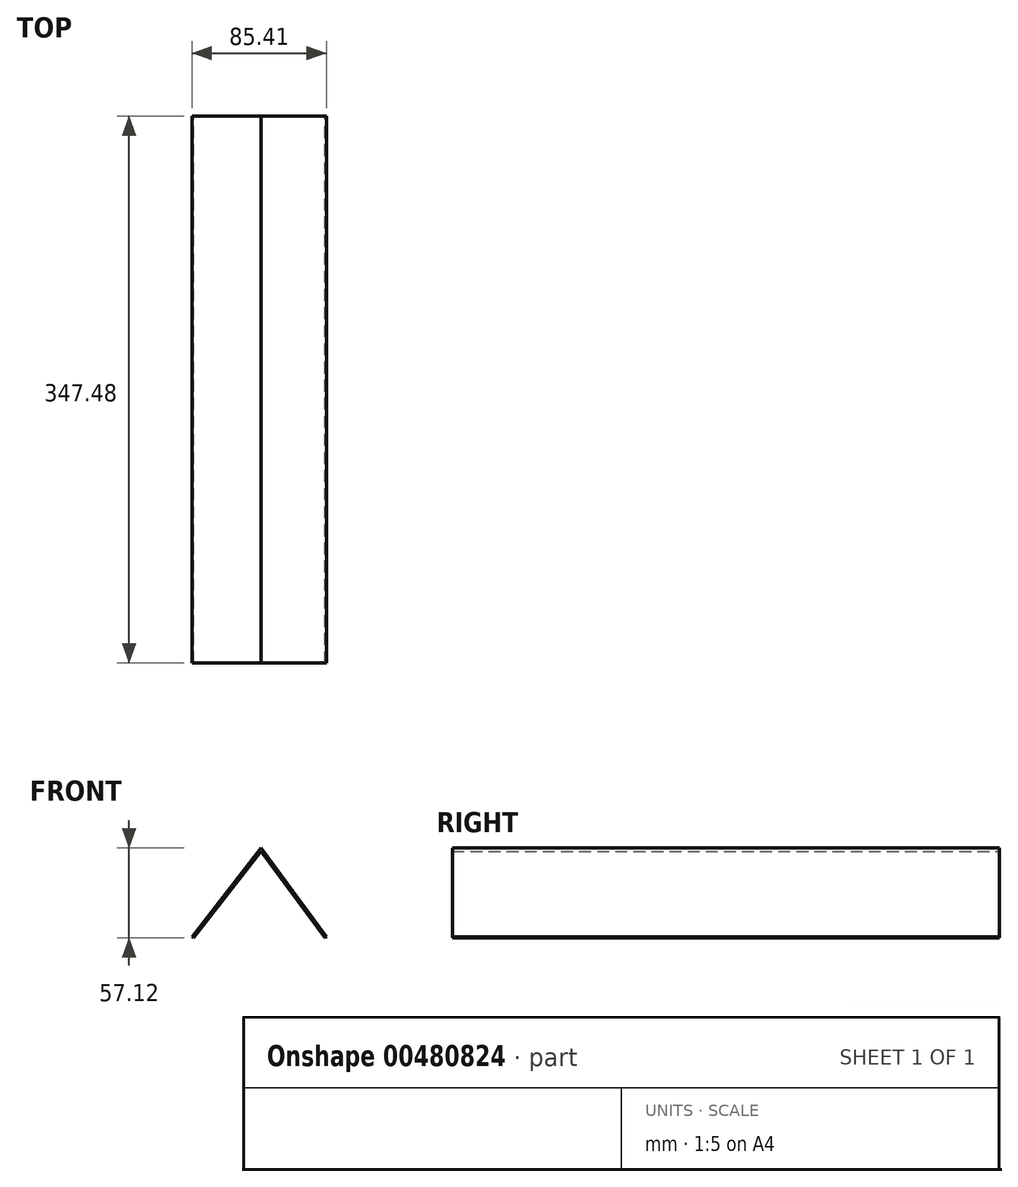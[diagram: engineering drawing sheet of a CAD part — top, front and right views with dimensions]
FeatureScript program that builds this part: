
annotation { "Feature Type Name" : "Feature", "Feature Type Description" : "" }
export const myFeature = defineFeature(function(context is Context, id is Id, definition is map)
    precondition{}
    {
        {
            var Q0;
            Q0=qCreatedBy(makeId("Front.planeOp"),FACE);
            var sketch = newSketch(context, id + "F0", { "sketchPlane" : qUnion([Q0])});
            skLineSegment(sketch, "E0", {"start": v(-44.02, 0) * mm, "end": v(0, 56.34) * mm});
            skLineSegment(sketch, "E1", {"start": v(0, 56.34) * mm, "end": v(41.39, 0) * mm});
            skLineSegment(sketch, "E2.0", {"start": v(-0.03, 54.24) * mm, "end": v(40.37, -0.75) * mm});
            skLineSegment(sketch, "E2.1", {"start": v(-43.02, -0.78) * mm, "end": v(-0.03, 54.24) * mm});
            skLineSegment(sketch, "E3", {"start": v(-43.02, -0.78) * mm, "end": v(-44.02, 0) * mm});
            skLineSegment(sketch, "E4", {"start": v(40.37, -0.75) * mm, "end": v(41.39, 0) * mm});
            skSolve(sketch);
        }
        {
            var Q0;
            Q0 = qSketchRegion(id + "F0", true);
            extrude(context, id + "F1", {"entities" : qUnion([Q0]), "endBound" : BoundingType.SYMMETRIC, "depth" : 347.47 * mm});
        }
    });
